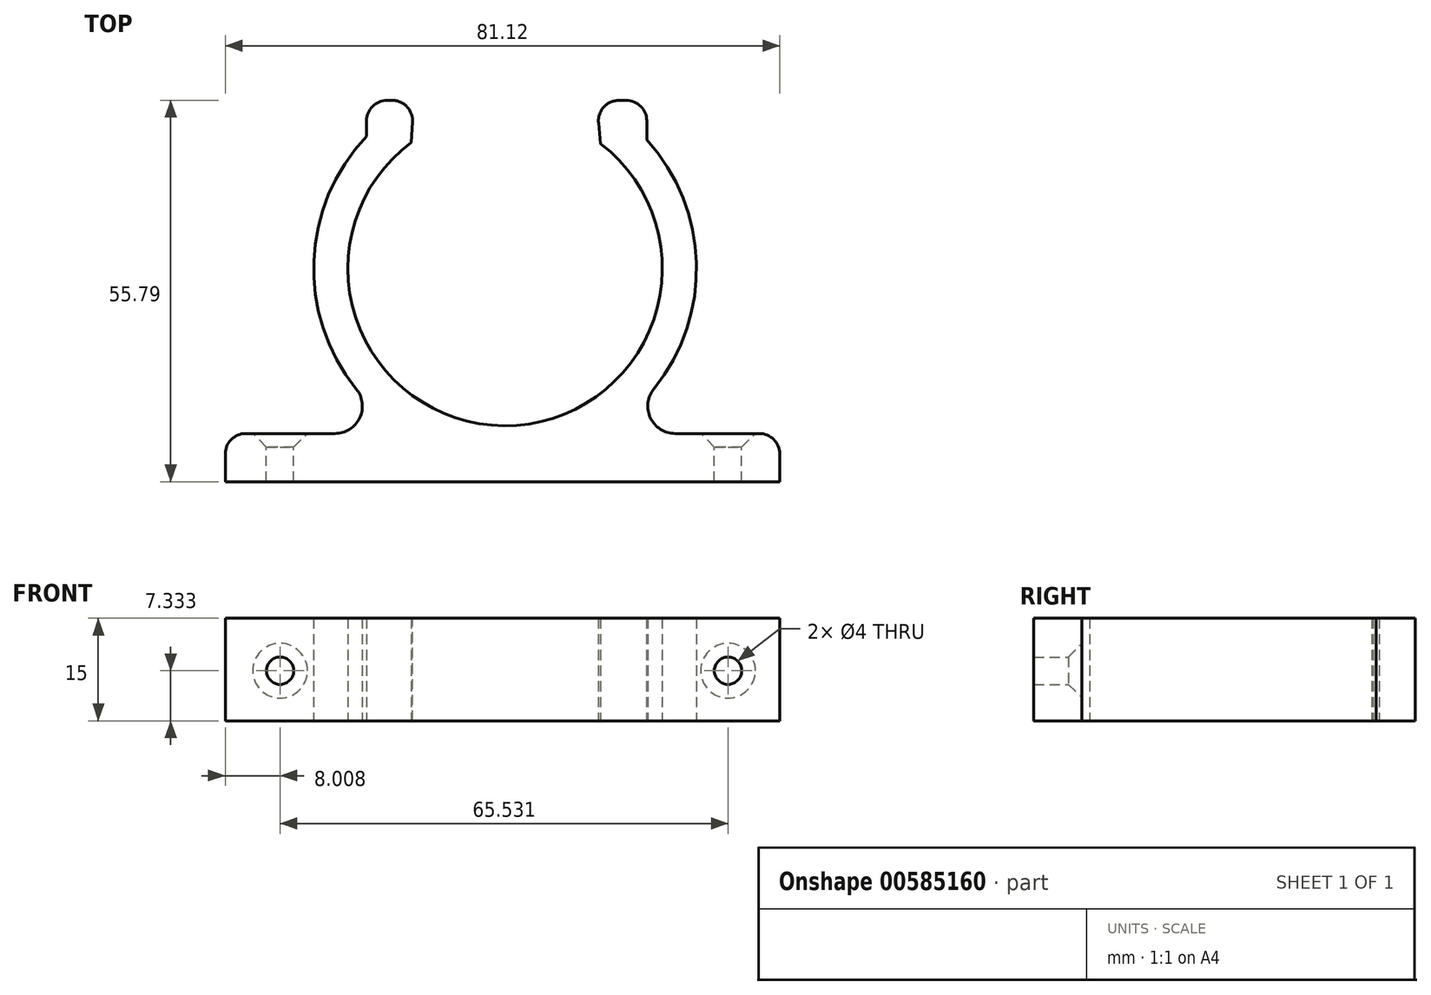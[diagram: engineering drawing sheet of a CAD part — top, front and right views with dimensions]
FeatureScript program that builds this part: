
annotation { "Feature Type Name" : "Feature", "Feature Type Description" : "" }
export const myFeature = defineFeature(function(context is Context, id is Id, definition is map)
    precondition{}
    {
        {
            var Q0;
            Q0=qCreatedBy(makeId("Top.planeOp"),FACE);
            var sketch = newSketch(context, id + "F0", { "sketchPlane" : qUnion([Q0])});
            skLineSegment(sketch, "E0.bottom", {"start": v(20.84, 30) * mm, "end": v(101.96, 30) * mm});
            skLineSegment(sketch, "E0.top", {"start": v(20.84, 37.05) * mm, "end": v(47.56, 37.05) * mm});
            skLineSegment(sketch, "E0.left", {"start": v(20.84, 30) * mm, "end": v(20.84, 37.05) * mm});
            skLineSegment(sketch, "E0.right", {"start": v(101.96, 30) * mm, "end": v(101.96, 37.05) * mm});
            skLineSegment(sketch, "E1", {"start": v(75.79, 37.05) * mm, "end": v(101.96, 37.05) * mm});
            skArc(sketch, "E2", {"start": v(47.12, 37.3) * mm, "mid": v(47.34, 37.18) * mm, "end": v(47.56, 37.05) * mm});
            skArc(sketch, "E3", {"start": v(75.97, 37.05) * mm, "mid": v(89.45, 57.02) * mm, "end": v(82.43, 80.07) * mm});
            skLineSegment(sketch, "E4.bottom", {"start": v(41.5, 85.79) * mm, "end": v(48.4, 85.79) * mm});
            skLineSegment(sketch, "E4.left", {"start": v(41.5, 85.79) * mm, "end": v(41.5, 80.08) * mm});
            skLineSegment(sketch, "E4.right", {"start": v(82.5, 85.79) * mm, "end": v(82.5, 80.07) * mm});
            skArc(sketch, "E5", {"start": v(75.73, 79.45) * mm, "mid": v(75.6, 79.55) * mm, "end": v(75.47, 79.65) * mm});
            skArc(sketch, "E6", {"start": v(48.06, 79.65) * mm, "mid": v(61.6, 38.18) * mm, "end": v(75.73, 79.45) * mm});
            skLineSegment(sketch, "E7.trimOffspring", {"start": v(82.43, 80.07) * mm, "end": v(82.5, 80.07) * mm});
            skArc(sketch, "E8.trimOffspring", {"start": v(41.5, 80.5) * mm, "mid": v(34, 57.57) * mm, "end": v(47.12, 37.3) * mm});
            skLineSegment(sketch, "E9.trimOffspring", {"start": v(75.12, 85.79) * mm, "end": v(82.5, 85.79) * mm});
            skLineSegment(sketch, "E10", {"start": v(48.06, 79.65) * mm, "end": v(48.4, 85.79) * mm});
            skLineSegment(sketch, "E11", {"start": v(75.73, 79.45) * mm, "end": v(75.12, 85.79) * mm});
            skSolve(sketch);
        }
        {
            var Q0;
            Q0 = qSketchRegion(id + "F0", true);
            extrude(context, id + "F1", {"entities" : qUnion([Q0]), "depth" : 15 * mm, "offsetDistance" : 25.4 * mm});
        }
        {
            var Q0;
            Q0=makeQuery(id+"F1.opExtrude","SWEPT_EDGE",EDGE,{"disambiguationData":[OSD([sQuery(id+"F0.wireOp",EDGE,"E9.trimOffspring"),sQuery(id+"F0.wireOp",EDGE,"E11")])]});
            var Q1;
            Q1=makeQuery(id+"F1.opExtrude","SWEPT_EDGE",EDGE,{"disambiguationData":[OSD([sQuery(id+"F0.wireOp",EDGE,"E4.right"),sQuery(id+"F0.wireOp",EDGE,"E9.trimOffspring")])]});
            var Q2;
            Q2=makeQuery(id+"F1.opExtrude","SWEPT_EDGE",EDGE,{"disambiguationData":[OSD([sQuery(id+"F0.wireOp",EDGE,"E4.bottom"),sQuery(id+"F0.wireOp",EDGE,"E10")])]});
            var Q3;
            Q3=makeQuery(id+"F1.opExtrude","SWEPT_EDGE",EDGE,{"disambiguationData":[OSD([sQuery(id+"F0.wireOp",EDGE,"E4.bottom"),sQuery(id+"F0.wireOp",EDGE,"E4.left")])]});
            var Q4;
            Q4=makeQuery(id+"F1.opExtrude","SWEPT_EDGE",EDGE,{"disambiguationData":[OSD([sQuery(id+"F0.wireOp",EDGE,"E0.top"),sQuery(id+"F0.wireOp",EDGE,"E0.left")])]});
            var Q5;
            Q5=makeQuery(id+"F1.opExtrude","SWEPT_EDGE",EDGE,{"disambiguationData":[OSD([sQuery(id+"F0.wireOp",EDGE,"E0.right"),sQuery(id+"F0.wireOp",EDGE,"E1")])]});
            fillet(context, id + "F2", {"entities" : qUnion([Q0, Q1, Q2, Q3, Q4, Q5]), "radius" : 3 * mm, "tangentPropagation" : true, "allowEdgeOverflow" : false});
        }
        {
            var Q0;
            Q0=makeQuery(id+"F1.opExtrude","SWEPT_FACE",FACE,{"disambiguationData":[OSD([sQuery(id+"F0.wireOp",EDGE,"E1")])]});
            var sketch = newSketch(context, id + "F3", { "sketchPlane" : qUnion([Q0])});
            skCircle(sketch, "E12", {"center": v(-94.38, 7.33) * mm, "radius": 5.5 * mm});
            skCircle(sketch, "E13", {"center": v(-28.85, 7.33) * mm, "radius": 5.5 * mm});
            skSolve(sketch);
        }
        {
            var Q0;
            Q0=sQuery(id+"F3.wireOp",VERTEX,"E12.center");
            var Q1;
            Q1=sQuery(id+"F3.wireOp",VERTEX,"E13.center");
            var Q2;
            Q2=makeQuery(id+"F1.opExtrude","SWEPT_BODY",BODY,{"disambiguationData":[OSD([sQuery(id+"F0.wireOp",EDGE,"E0.bottom"),sQuery(id+"F0.wireOp",EDGE,"E0.top"),sQuery(id+"F0.wireOp",EDGE,"E0.left"),sQuery(id+"F0.wireOp",EDGE,"E0.right"),sQuery(id+"F0.wireOp",EDGE,"E1"),sQuery(id+"F0.wireOp",EDGE,"E2"),sQuery(id+"F0.wireOp",EDGE,"E3"),sQuery(id+"F0.wireOp",EDGE,"E4.bottom"),sQuery(id+"F0.wireOp",EDGE,"E4.left"),sQuery(id+"F0.wireOp",EDGE,"E4.right"),sQuery(id+"F0.wireOp",EDGE,"E6"),sQuery(id+"F0.wireOp",EDGE,"E7.trimOffspring"),sQuery(id+"F0.wireOp",EDGE,"E8.trimOffspring"),sQuery(id+"F0.wireOp",EDGE,"E9.trimOffspring"),sQuery(id+"F0.wireOp",EDGE,"E10"),sQuery(id+"F0.wireOp",EDGE,"E11")])]});
            hole(context, id + "F4", {"style" : HoleStyle.C_SINK, "endStyle" : HoleEndStyle.THROUGH, "holeDiameter" : 4 * mm, "cSinkDiameter" : 8 * mm, "cSinkAngle" : 90 * degree, "majorDiameter" : 5 * mm, "isTappedThrough" : true, "tappedDepth" : 12 * mm, "tapClearance" : 3, "locations" : qUnion([Q0, Q1]), "scope" : qUnion([Q2])});
        }
        {
            var Q0;
            Q0=makeQuery(id+"F1.opExtrude","SWEPT_EDGE",EDGE,{"disambiguationData":[OSD([sQuery(id+"F0.wireOp",EDGE,"E1"),sQuery(id+"F0.wireOp",EDGE,"E3")])]});
            var Q1;
            Q1=makeQuery(id+"F1.opExtrude","SWEPT_EDGE",EDGE,{"disambiguationData":[OSD([sQuery(id+"F0.wireOp",EDGE,"E0.top"),sQuery(id+"F0.wireOp",EDGE,"E2")])]});
            fillet(context, id + "F5", {"entities" : qUnion([Q0, Q1]), "radius" : 4 * mm, "tangentPropagation" : true, "allowEdgeOverflow" : false});
        }
    });
